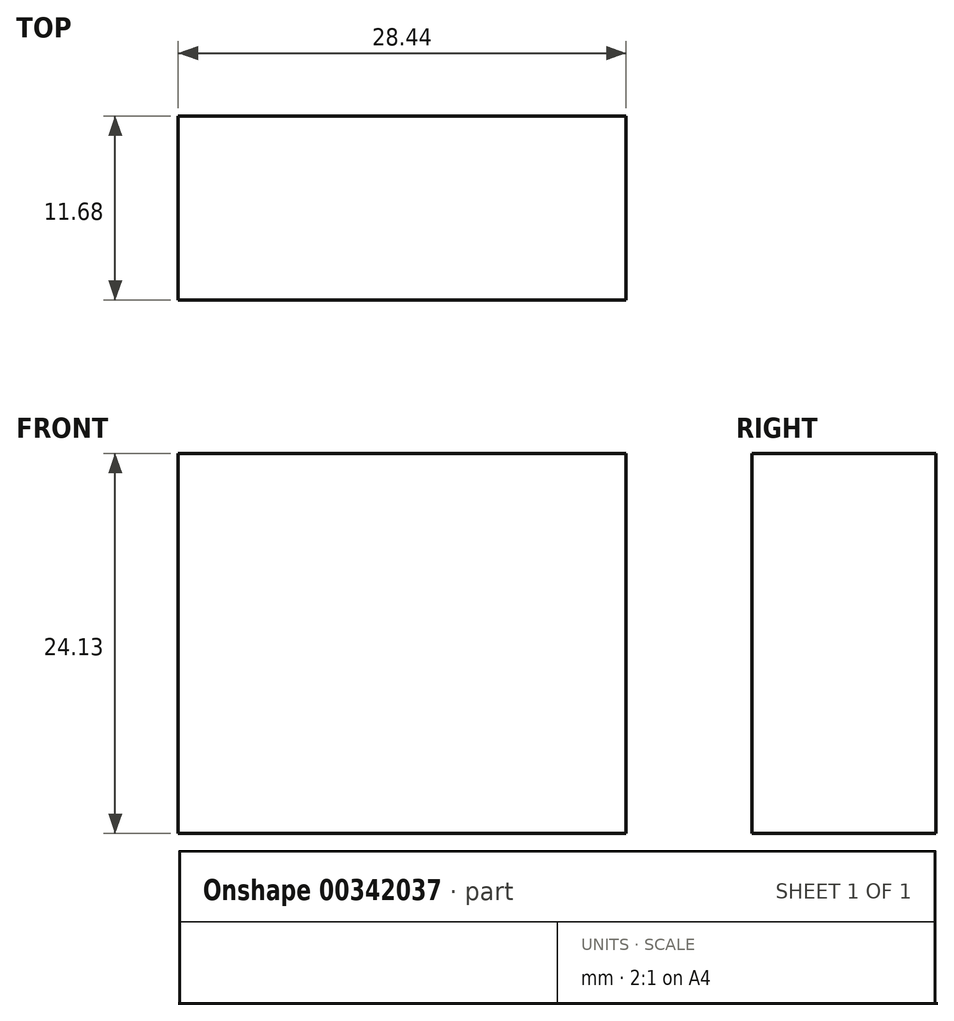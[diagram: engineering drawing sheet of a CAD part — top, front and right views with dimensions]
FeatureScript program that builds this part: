
annotation { "Feature Type Name" : "Feature", "Feature Type Description" : "" }
export const myFeature = defineFeature(function(context is Context, id is Id, definition is map)
    precondition{}
    {
        {
            var Q0;
            Q0=qCreatedBy(makeId("Front.planeOp"),FACE);
            var sketch = newSketch(context, id + "F0", { "sketchPlane" : qUnion([Q0])});
            skLineSegment(sketch, "E0.bottom", {"start": v(-12.48, 15.67) * mm, "end": v(15.96, 15.67) * mm});
            skLineSegment(sketch, "E0.top", {"start": v(-12.48, -8.46) * mm, "end": v(15.96, -8.46) * mm});
            skLineSegment(sketch, "E0.left", {"start": v(-12.48, 15.67) * mm, "end": v(-12.48, -8.46) * mm});
            skLineSegment(sketch, "E0.right", {"start": v(15.96, 15.67) * mm, "end": v(15.96, -8.46) * mm});
            skSolve(sketch);
        }
        {
            var Q0;
            Q0=makeQuery(id+"F0.imprint","IMPRINT",FACE,{"disambiguationData":[TD([[makeQuery(id+"F0.imprint","IMPRINT",EDGE,{"derivedFrom":sQuery(id+"F0.wireOp",EDGE,"E0.bottom")}),-1.0]])]});
            extrude(context, id + "F1", {"entities" : qUnion([Q0]), "depth" : 11.68 * mm});
        }
    });
